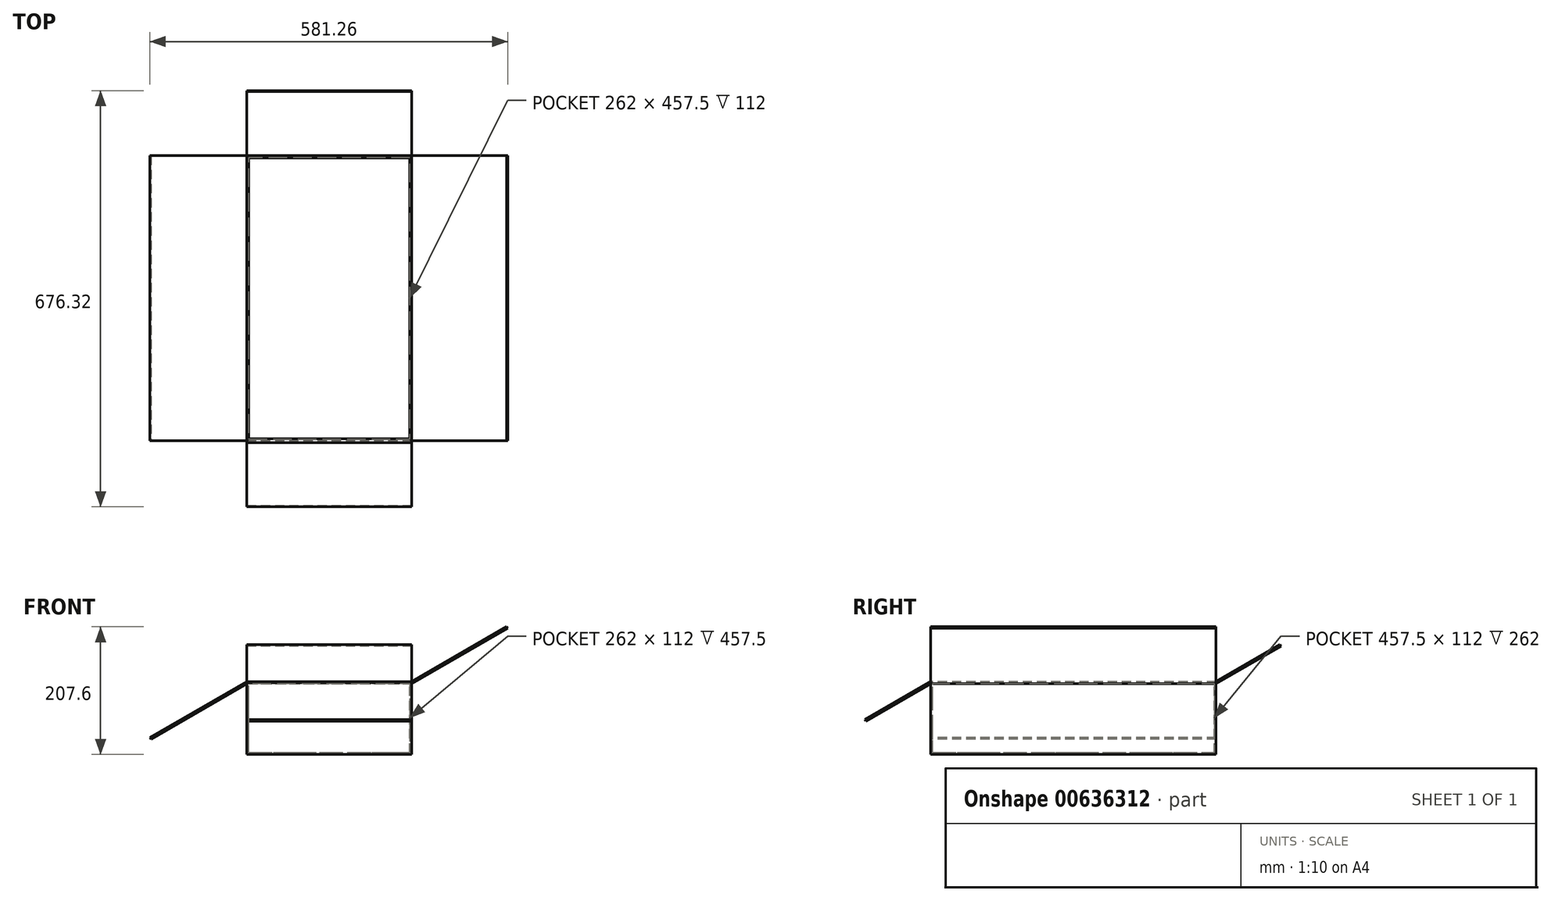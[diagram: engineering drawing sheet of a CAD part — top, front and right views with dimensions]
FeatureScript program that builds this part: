
annotation { "Feature Type Name" : "Feature", "Feature Type Description" : "" }
export const myFeature = defineFeature(function(context is Context, id is Id, definition is map)
    precondition{}
    {
        {
            var Q0;
            Q0=qCreatedBy(makeId("Front.planeOp"),FACE);
            var sketch = newSketch(context, id + "F0", { "sketchPlane" : qUnion([Q0])});
            skLineSegment(sketch, "E0.bottom", {"start": v(0, 0) * mm, "end": v(268, 0) * mm});
            skLineSegment(sketch, "E0.top", {"start": v(0, 115) * mm, "end": v(268, 115) * mm});
            skLineSegment(sketch, "E0.left", {"start": v(0, 0) * mm, "end": v(0, 115) * mm});
            skLineSegment(sketch, "E0.right", {"start": v(268, 0) * mm, "end": v(268, 115) * mm});
            skSolve(sketch);
        }
        {
            var Q0;
            Q0=qSketchRegion(id+"F0",true);
            extrude(context, id + "F1", {"entities" : qUnion([Q0]), "depth" : 463.5 * mm, "offsetDistance" : 25 * mm});
        }
        {
            var Q0;
            Q0=makeQuery(id+"F1.opExtrude","SWEPT_FACE",FACE,{"disambiguationData":[OSD([sQuery(id+"F0.wireOp",EDGE,"E0.top")])]});
            shell(context, id + "F2", {"entities" : qUnion([Q0]), "thickness" : 3 * mm});
        }
        {
            var Q0;
            Q0=makeQuery(id+"F1.opExtrude","CAP_FACE",FACE,{"disambiguationData":[OSD([sQuery(id+"F0.wireOp",EDGE,"E0.bottom"),sQuery(id+"F0.wireOp",EDGE,"E0.top"),sQuery(id+"F0.wireOp",EDGE,"E0.left"),sQuery(id+"F0.wireOp",EDGE,"E0.right")])],"isStart":false});
            var sketch = newSketch(context, id + "F3", { "sketchPlane" : qUnion([Q0])});
            skLineSegment(sketch, "E1", {"start": v(0, 115) * mm, "end": v(-155.88, 25) * mm});
            skLineSegment(sketch, "E2", {"start": v(-155.88, 25) * mm, "end": v(-157.38, 27.6) * mm});
            skLineSegment(sketch, "E3", {"start": v(-157.38, 27.6) * mm, "end": v(0, 118.46) * mm});
            skArc(sketch, "E4", {"start": v(0, 118.46) * mm, "mid": v(2.45, 117.45) * mm, "end": v(3.46, 115) * mm});
            skLineSegment(sketch, "E5", {"start": v(268, 115) * mm, "end": v(423.88, 205) * mm});
            skLineSegment(sketch, "E6", {"start": v(423.88, 205) * mm, "end": v(422.38, 207.6) * mm});
            skLineSegment(sketch, "E7", {"start": v(422.38, 207.6) * mm, "end": v(268, 118.46) * mm});
            skArc(sketch, "E8", {"start": v(268, 118.46) * mm, "mid": v(265.55, 117.45) * mm, "end": v(264.54, 115) * mm});
            skLineSegment(sketch, "E9", {"start": v(0, 115) * mm, "end": v(3.46, 115) * mm});
            skLineSegment(sketch, "E10", {"start": v(264.54, 115) * mm, "end": v(268, 115) * mm});
            skSolve(sketch);
        }
        {
            var Q0;
            Q0=qSketchRegion(id+"F3",true);
            var Q1;
            Q1=makeQuery(id+"F1.opExtrude","CAP_FACE",FACE,{"disambiguationData":[OSD([sQuery(id+"F0.wireOp",EDGE,"E0.bottom"),sQuery(id+"F0.wireOp",EDGE,"E0.top"),sQuery(id+"F0.wireOp",EDGE,"E0.left"),sQuery(id+"F0.wireOp",EDGE,"E0.right")])],"isStart":true});
            extrude(context, id + "F4", {"entities" : qUnion([Q0]), "operationType" : NewBodyOperationType.ADD, "endBound" : BoundingType.UP_TO_SURFACE, "oppositeDirection" : true, "depth" : 216 * mm, "endBoundEntityFace" : qUnion([Q1]), "offsetDistance" : 25 * mm});
        }
        {
            var Q0;
            Q0=makeQuery(id+"F1.opExtrude","SWEPT_FACE",FACE,{"disambiguationData":[OSD([sQuery(id+"F0.wireOp",EDGE,"E0.left")])]});
            var sketch = newSketch(context, id + "F5", { "sketchPlane" : qUnion([Q0])});
            skLineSegment(sketch, "E11", {"start": v(463.5, 115) * mm, "end": v(569.16, 54) * mm});
            skLineSegment(sketch, "E12", {"start": v(569.16, 54) * mm, "end": v(570.66, 56.6) * mm});
            skLineSegment(sketch, "E13", {"start": v(570.66, 56.6) * mm, "end": v(466.5, 116.73) * mm});
            skLineSegment(sketch, "E14", {"start": v(460.04, 115) * mm, "end": v(463.5, 115) * mm});
            skLineSegment(sketch, "E15", {"start": v(0, 115) * mm, "end": v(-105.66, 176) * mm});
            skLineSegment(sketch, "E16", {"start": v(-105.66, 176) * mm, "end": v(-104.16, 178.6) * mm});
            skLineSegment(sketch, "E17", {"start": v(-104.16, 178.6) * mm, "end": v(0, 118.46) * mm});
            skArc(sketch, "E18", {"start": v(0, 118.46) * mm, "mid": v(2.45, 117.45) * mm, "end": v(3.46, 115) * mm});
            skLineSegment(sketch, "E19", {"start": v(0, 115) * mm, "end": v(3.46, 115) * mm});
            skPoint(sketch, "E20.0", {"position": v(463.5, 118.46) * mm});
            skArc(sketch, "E21", {"start": v(463.5, 118.46) * mm, "mid": v(461.05, 117.45) * mm, "end": v(460.04, 115) * mm});
            skArc(sketch, "E22", {"start": v(463.5, 118.46) * mm, "mid": v(465.23, 118) * mm, "end": v(466.5, 116.73) * mm});
            skSolve(sketch);
        }
        {
            var Q0;
            Q0=qSketchRegion(id+"F5",true);
            var Q1;
            Q1=makeQuery(id+"F1.opExtrude","SWEPT_FACE",FACE,{"disambiguationData":[OSD([sQuery(id+"F0.wireOp",EDGE,"E0.right")])]});
            extrude(context, id + "F6", {"entities" : qUnion([Q0]), "operationType" : NewBodyOperationType.ADD, "endBound" : BoundingType.UP_TO_SURFACE, "oppositeDirection" : true, "depth" : 25 * mm, "endBoundEntityFace" : qUnion([Q1]), "offsetDistance" : 25 * mm});
        }
    });
